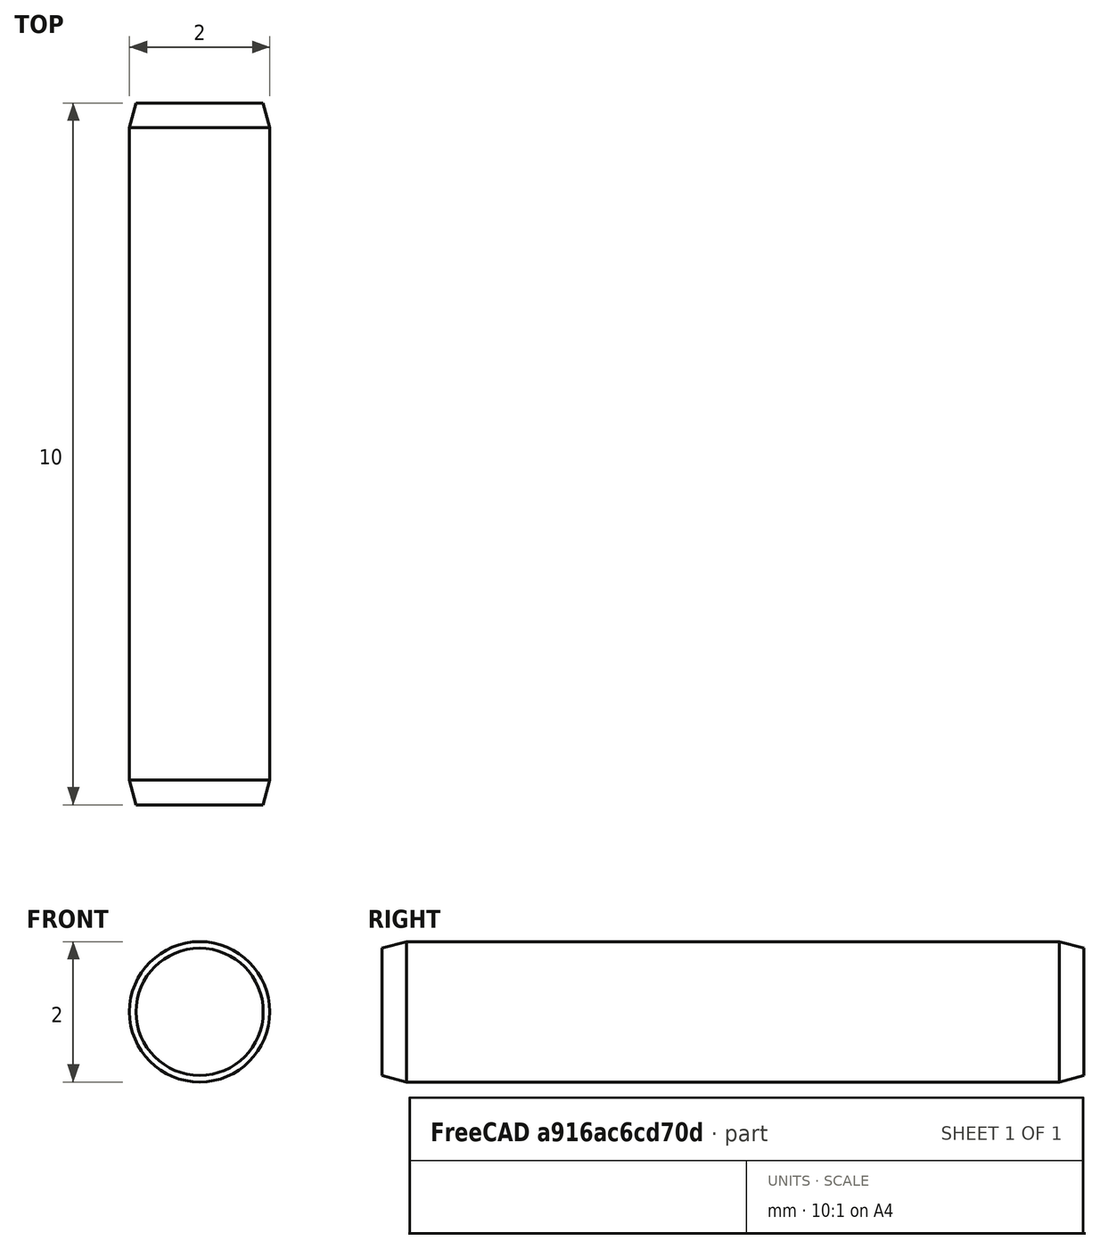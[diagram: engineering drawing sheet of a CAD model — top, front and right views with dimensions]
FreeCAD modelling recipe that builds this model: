
FCSTD DOCUMENT  (FreeCAD 0.15R4470 (Git))
Label: Zyl-Stift_ISO_8734-2x10
License: CC-BY 3.0
LicenseURL: http://creativecommons.org/licenses/by/3.0/
objects: Sketcher::SketchObject×1, PartDesign::Revolution×1
note: 3 computed .brp shape members not serialized (recipe doc carries the construction recipe); baked Part::Feature solids carry a one-line shape summary decoded from their .brp

FEATURE [Sketcher::SketchObject] Sketch
  Placement = pos=(0,0,0) rot=(0.57735,0.57735,0.57735;2.0944rad)
  sketch-geometry (7):
    g0: LineSegment StartX=0 StartY=0 StartZ=0 EndX=0 EndY=0.906218 EndZ=0
    g1: LineSegment StartX=0 StartY=0.906218 StartZ=0 EndX=0.35 EndY=1 EndZ=0
    g2: LineSegment StartX=0.35 StartY=1 StartZ=0 EndX=9.65 EndY=1 EndZ=0
    g3: LineSegment StartX=9.65 StartY=1 StartZ=0 EndX=10 EndY=0.906218 EndZ=0
    g4: LineSegment StartX=10 StartY=0.906218 StartZ=0 EndX=10 EndY=0 EndZ=0
    g5: LineSegment StartX=10 StartY=0 StartZ=0 EndX=0 EndY=0 EndZ=0
    g6: LineSegment [constr] StartX=0 StartY=0.906218 StartZ=0 EndX=10 EndY=0.906218 EndZ=0
  constraints (19):
    c: Coincident(g0,g-1)
    c: PointOnObject(g0,g-2)
    c: Coincident(g0,g1)
    c: Coincident(g1,g2)
    c: Horizontal(g2)
    c: Coincident(g2,g3)
    c: Coincident(g3,g4)
    c: Vertical(g4)
    c: Coincident(g4,g5)
    c: Coincident(g5,g-1)
    c: Horizontal(g5)
    c: Equal(g3,g1)
    c: Coincident(g6,g0)
    c: Coincident(g6,g3)
    c: Horizontal(g6)
    c: Angle(g6,g1) = 0.261799
    c: DistanceY(g-1,g1) = 1
    c: DistanceX(g5) = -10
    c: DistanceX(g1) = 0.35
FEATURE [PartDesign::Revolution] Revolution  label="Zyl-Stift ISO 8734-2x10 #"
  Angle = 360
  Axis = (0,1,0)
  Base = (0,0,0)
  Placement = pos=(0,0,0) rot=(0.57735,0.57735,0.57735;2.0944rad)
  ReferenceAxis = -> Sketch [H_Axis]
  Sketch = -> Sketch
